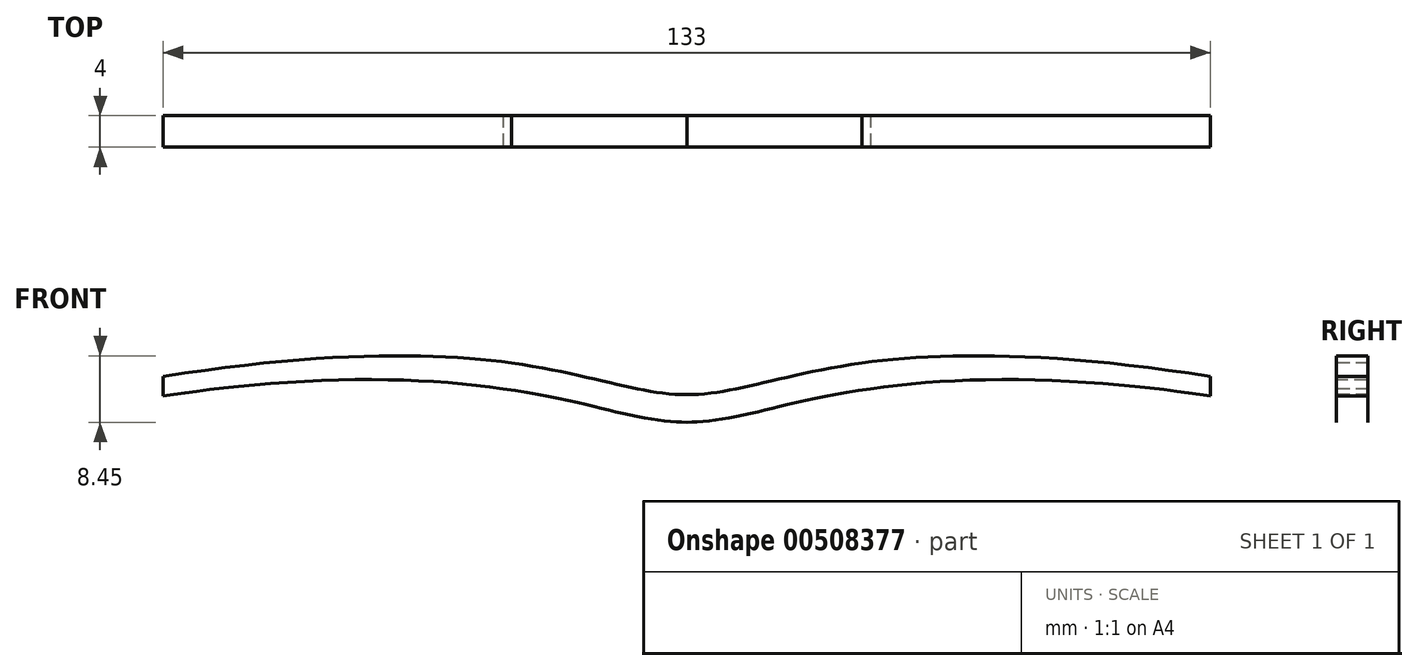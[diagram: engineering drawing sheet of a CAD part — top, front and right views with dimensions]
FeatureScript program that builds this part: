
annotation { "Feature Type Name" : "Feature", "Feature Type Description" : "" }
export const myFeature = defineFeature(function(context is Context, id is Id, definition is map)
    precondition{}
    {
        {
            var Q0;
            Q0=qCreatedBy(makeId("Front.planeOp"),FACE);
            var sketch = newSketch(context, id + "F0", { "sketchPlane" : qUnion([Q0])});
            skFitSpline(sketch, "E0", {"points": [v(-67.59, 3.24) * mm, v(0, 0) * mm, v(66.5, 2.32) * mm], "startDerivative": vector(268.98, 35.93) * mm, "endDerivative": vector(268.84, -42.23) * mm});
            skLineSegment(sketch, "E1", {"start": v(66.5, 2.32) * mm, "end": v(66.5, -6.01) * mm});
            skLineSegment(sketch, "E2", {"start": v(66.5, -6.01) * mm, "end": v(65.36, -6.66) * mm});
            skLineSegment(sketch, "E3", {"start": v(63.05, -9.55) * mm, "end": v(58.2, -25.45) * mm});
            skFitSpline(sketch, "E4", {"points": [v(58.2, -25.45) * mm, v(42.49, -38.37) * mm, v(13.07, -31.3) * mm, v(3.6, -10.05) * mm, v(0, -9) * mm], "startDerivative": vector(-33.46, -102.86) * mm, "endDerivative": vector(-19.85, 0) * mm});
            skLineSegment(sketch, "E5", {"start": v(0, -9) * mm, "end": v(0, 0) * mm, "construction": true});
            skLineSegment(sketch, "E6", {"start": v(0, -9) * mm, "end": v(4.16, -9) * mm, "construction": true});
            skPoint(sketch, "E7.visualSharp", {"position": v(63.63, -7.65) * mm});
            skArc(sketch, "E7.filletArc", {"start": v(65.36, -6.66) * mm, "mid": v(63.93, -7.89) * mm, "end": v(63.05, -9.55) * mm});
            skFitSpline(sketch, "E8.MirrorCS", {"points": [v(67.59, 3.24) * mm, v(0, 0) * mm, v(-66.5, 2.32) * mm], "startDerivative": vector(-268.98, 35.93) * mm, "endDerivative": vector(-268.84, -42.23) * mm});
            skLineSegment(sketch, "E9.MirrorCS", {"start": v(-66.5, 2.32) * mm, "end": v(-66.5, -6.01) * mm});
            skLineSegment(sketch, "E10.MirrorCS", {"start": v(-66.5, -6.01) * mm, "end": v(-65.36, -6.66) * mm});
            skArc(sketch, "E11.MirrorCS", {"start": v(-65.36, -6.66) * mm, "mid": v(-63.93, -7.89) * mm, "end": v(-63.05, -9.55) * mm});
            skLineSegment(sketch, "E12.MirrorCS", {"start": v(-63.05, -9.55) * mm, "end": v(-58.2, -25.45) * mm});
            skFitSpline(sketch, "E13.MirrorCS", {"points": [v(-58.2, -25.45) * mm, v(-42.49, -38.37) * mm, v(-13.07, -31.3) * mm, v(-3.6, -10.05) * mm, v(0, -9) * mm], "startDerivative": vector(33.46, -102.86) * mm, "endDerivative": vector(19.85, 0) * mm});
            skFitSpline(sketch, "E14.0", {"points": [v(54.87, -24.37) * mm, v(54.56, -25.33) * mm, v(53.9, -27.06) * mm, v(52.8, -29.1) * mm, v(51.66, -30.68) * mm, v(50.43, -31.88) * mm, v(49.07, -32.83) * mm, v(47.5, -33.6) * mm, v(45.65, -34.21) * mm, v(43.86, -34.6) * mm, v(42.27, -34.87) * mm, v(40.58, -35.1) * mm, v(38.35, -35.3) * mm, v(35.55, -35.41) * mm, v(31.7, -35.33) * mm, v(26.9, -34.77) * mm, v(22.5, -33.5) * mm, v(19.45, -32.04) * mm, v(17.8, -30.95) * mm, v(16.63, -29.96) * mm, v(15.96, -29.3) * mm, v(15.47, -28.74) * mm, v(15, -28.15) * mm, v(14.43, -27.35) * mm, v(13.8, -26.3) * mm, v(13, -24.8) * mm, v(12.12, -22.76) * mm, v(11.2, -20.17) * mm, v(10.4, -17.54) * mm, v(9.64, -14.97) * mm, v(9, -12.94) * mm, v(8.42, -11.4) * mm, v(7.94, -10.3) * mm, v(7.46, -9.4) * mm, v(7.01, -8.7) * mm, v(6.63, -8.19) * mm, v(6.26, -7.77) * mm, v(5.93, -7.44) * mm, v(5.6, -7.13) * mm, v(5.15, -6.8) * mm, v(4.42, -6.33) * mm, v(3.5, -5.92) * mm, v(2.48, -5.65) * mm, v(1.58, -5.52) * mm, v(0.82, -5.49) * mm, v(0.25, -5.5) * mm, v(0.03, -5.5) * mm, v(0, -5.5) * mm]});
            skFitSpline(sketch, "E15.0", {"points": [v(-67.12, -0.23) * mm, v(-61.59, 0.51) * mm, v(-51.57, 1.52) * mm, v(-39.31, 1.9) * mm, v(-29.43, 1.45) * mm, v(-21.51, 0.46) * mm, v(-15.11, -0.8) * mm, v(-10.65, -1.88) * mm, v(-7.36, -2.62) * mm, v(-4.96, -3.09) * mm, v(-2.97, -3.36) * mm, v(-1.36, -3.48) * mm, v(-0.15, -3.51) * mm, v(1.08, -3.48) * mm, v(2.68, -3.36) * mm, v(4.65, -3.1) * mm, v(7.02, -2.63) * mm, v(9.44, -2.07) * mm, v(11.98, -1.47) * mm, v(15.63, -0.63) * mm, v(20.82, 0.38) * mm, v(28.57, 1.28) * mm, v(38.3, 1.57) * mm, v(50.45, 0.95) * mm, v(60.43, -0.27) * mm, v(65.96, -1.14) * mm]});
            skFitSpline(sketch, "E16", {"points": [v(11.93, -22.17) * mm, v(19.05, 0) * mm], "startDerivative": vector(-6.54, 17.45) * mm, "endDerivative": vector(40.86, 7.1) * mm});
            skLineSegment(sketch, "E17", {"start": v(19.05, 0) * mm, "end": v(9.71, -1.62) * mm, "construction": true});
            skLineSegment(sketch, "E18", {"start": v(11.93, -22.17) * mm, "end": v(8.98, -14.3) * mm, "construction": true});
            skLineSegment(sketch, "E19", {"start": v(54.87, -24.37) * mm, "end": v(61.17, -5) * mm, "construction": true});
            skLineSegment(sketch, "E20", {"start": v(50, 0.83) * mm, "end": v(63.17, -0.13) * mm, "construction": true});
            skFitSpline(sketch, "E21", {"points": [v(54.87, -24.37) * mm, v(57.2, -3.73) * mm], "startDerivative": vector(7.97, 24.51) * mm, "endDerivative": vector(-1.54, 3.97) * mm});
            skFitSpline(sketch, "E22", {"points": [v(50, 0.83) * mm, v(57.2, -3.73) * mm], "startDerivative": vector(11.72, -0.85) * mm, "endDerivative": vector(2.29, -8.41) * mm});
            skLineSegment(sketch, "E23", {"start": v(57.71, -5.05) * mm, "end": v(56.44, -0.93) * mm, "construction": true});
            skFitSpline(sketch, "E24.MirrorCS", {"points": [v(-11.93, -22.17) * mm, v(-19.05, 0) * mm], "startDerivative": vector(6.54, 17.45) * mm, "endDerivative": vector(-40.86, 7.1) * mm});
            skFitSpline(sketch, "E25.MirrorCS", {"points": [v(-50, 0.83) * mm, v(-57.2, -3.73) * mm], "startDerivative": vector(-11.72, -0.85) * mm, "endDerivative": vector(-2.29, -8.41) * mm});
            skFitSpline(sketch, "E26.MirrorCS", {"points": [v(-54.87, -24.37) * mm, v(-57.2, -3.73) * mm], "startDerivative": vector(-7.97, 24.51) * mm, "endDerivative": vector(1.54, 3.97) * mm});
            skFitSpline(sketch, "E27.0", {"points": [v(-54.87, -24.37) * mm, v(-54.56, -25.33) * mm, v(-53.9, -27.06) * mm, v(-52.8, -29.1) * mm, v(-51.66, -30.68) * mm, v(-50.43, -31.88) * mm, v(-49.07, -32.83) * mm, v(-47.5, -33.6) * mm, v(-45.65, -34.21) * mm, v(-43.86, -34.6) * mm, v(-42.27, -34.87) * mm, v(-40.58, -35.1) * mm, v(-38.35, -35.3) * mm, v(-35.55, -35.41) * mm, v(-31.7, -35.33) * mm, v(-26.9, -34.77) * mm, v(-22.5, -33.5) * mm, v(-19.45, -32.04) * mm, v(-17.8, -30.95) * mm, v(-16.63, -29.96) * mm, v(-15.96, -29.3) * mm, v(-15.47, -28.74) * mm, v(-15, -28.15) * mm, v(-14.43, -27.35) * mm, v(-13.8, -26.3) * mm, v(-13, -24.8) * mm, v(-12.12, -22.76) * mm, v(-11.2, -20.17) * mm, v(-10.4, -17.54) * mm, v(-9.64, -14.97) * mm, v(-9, -12.94) * mm, v(-8.42, -11.4) * mm, v(-7.94, -10.3) * mm, v(-7.46, -9.4) * mm, v(-7.01, -8.7) * mm, v(-6.63, -8.19) * mm, v(-6.26, -7.77) * mm, v(-5.93, -7.44) * mm, v(-5.6, -7.13) * mm, v(-5.15, -6.8) * mm, v(-4.42, -6.33) * mm, v(-3.5, -5.92) * mm, v(-2.48, -5.65) * mm, v(-1.58, -5.52) * mm, v(-0.82, -5.49) * mm, v(-0.25, -5.5) * mm, v(-0.03, -5.5) * mm, v(0, -5.5) * mm]});
            skFitSpline(sketch, "E28.0", {"points": [v(67.12, -0.23) * mm, v(61.59, 0.51) * mm, v(51.57, 1.52) * mm, v(39.31, 1.9) * mm, v(29.43, 1.45) * mm, v(21.51, 0.46) * mm, v(15.11, -0.8) * mm, v(10.65, -1.88) * mm, v(7.36, -2.62) * mm, v(4.96, -3.09) * mm, v(2.97, -3.36) * mm, v(1.36, -3.48) * mm, v(0.15, -3.51) * mm, v(-1.08, -3.48) * mm, v(-2.68, -3.36) * mm, v(-4.65, -3.1) * mm, v(-7.02, -2.63) * mm, v(-9.44, -2.07) * mm, v(-11.98, -1.47) * mm, v(-15.63, -0.63) * mm, v(-20.82, 0.38) * mm, v(-28.57, 1.28) * mm, v(-38.3, 1.57) * mm, v(-50.45, 0.95) * mm, v(-60.43, -0.27) * mm, v(-65.96, -1.14) * mm]});
            skSolve(sketch);
        }
        {
            var Q0;
            Q0=makeQuery(id+"F0.imprint","IMPRINT",FACE,{"disambiguationData":[TD([[makeQuery(id+"F0.imprint","IMPRINT",EDGE,{"derivedFrom":sQuery(id+"F0.wireOp",EDGE,"E0")}),-1.0]])]});
            extrude(context, id + "F1", {"entities" : qUnion([Q0]), "oppositeDirection" : true, "depth" : 4 * mm});
        }
    });
